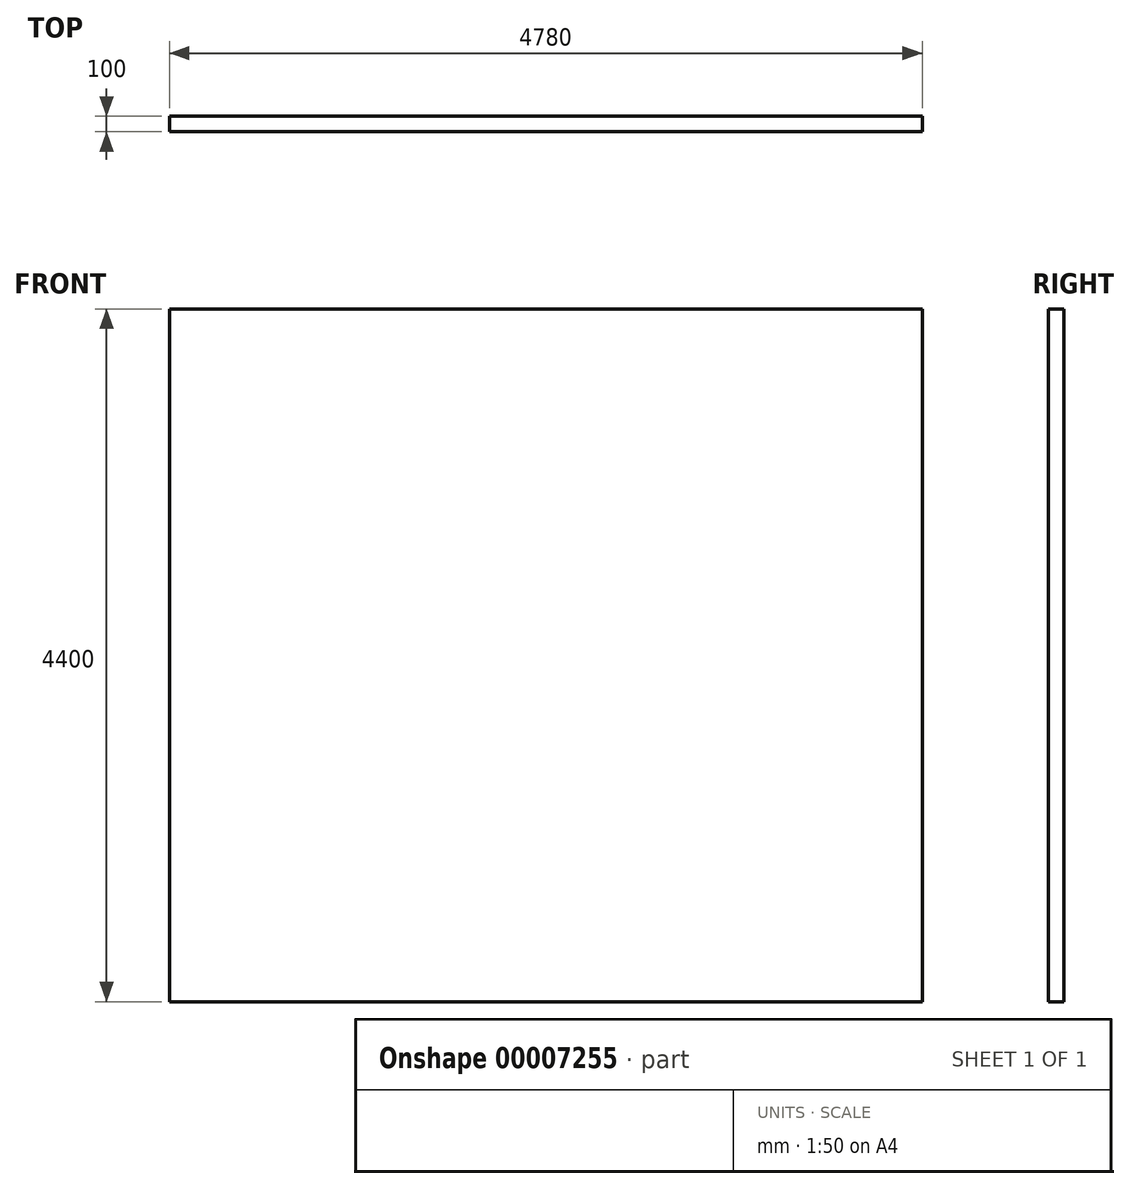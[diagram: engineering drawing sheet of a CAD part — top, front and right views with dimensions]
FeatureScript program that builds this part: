
annotation { "Feature Type Name" : "Feature", "Feature Type Description" : "" }
export const myFeature = defineFeature(function(context is Context, id is Id, definition is map)
    precondition{}
    {
        {
            var Q0;
            Q0=qCreatedBy(makeId("Front.planeOp"),FACE);
            var sketch = newSketch(context, id + "F0", { "sketchPlane" : qUnion([Q0])});
            skLineSegment(sketch, "E0", {"start": v(0, 0) * mm, "end": v(4780, 0) * mm});
            skLineSegment(sketch, "E1", {"start": v(4780, 0) * mm, "end": v(4780, 4400) * mm});
            skLineSegment(sketch, "E2", {"start": v(4780, 4400) * mm, "end": v(0, 4400) * mm});
            skLineSegment(sketch, "E3", {"start": v(0, 4400) * mm, "end": v(0, 0) * mm});
            skSolve(sketch);
        }
        {
            var Q0;
            Q0=makeQuery(id+"F0.imprint","IMPRINT",FACE,{"disambiguationData":[TD([[makeQuery(id+"F0.imprint","IMPRINT",EDGE,{"derivedFrom":sQuery(id+"F0.wireOp",EDGE,"E0")}),1.0]])]});
            extrude(context, id + "F1", {"entities" : qUnion([Q0]), "depth" : 100 * mm});
        }
    });
